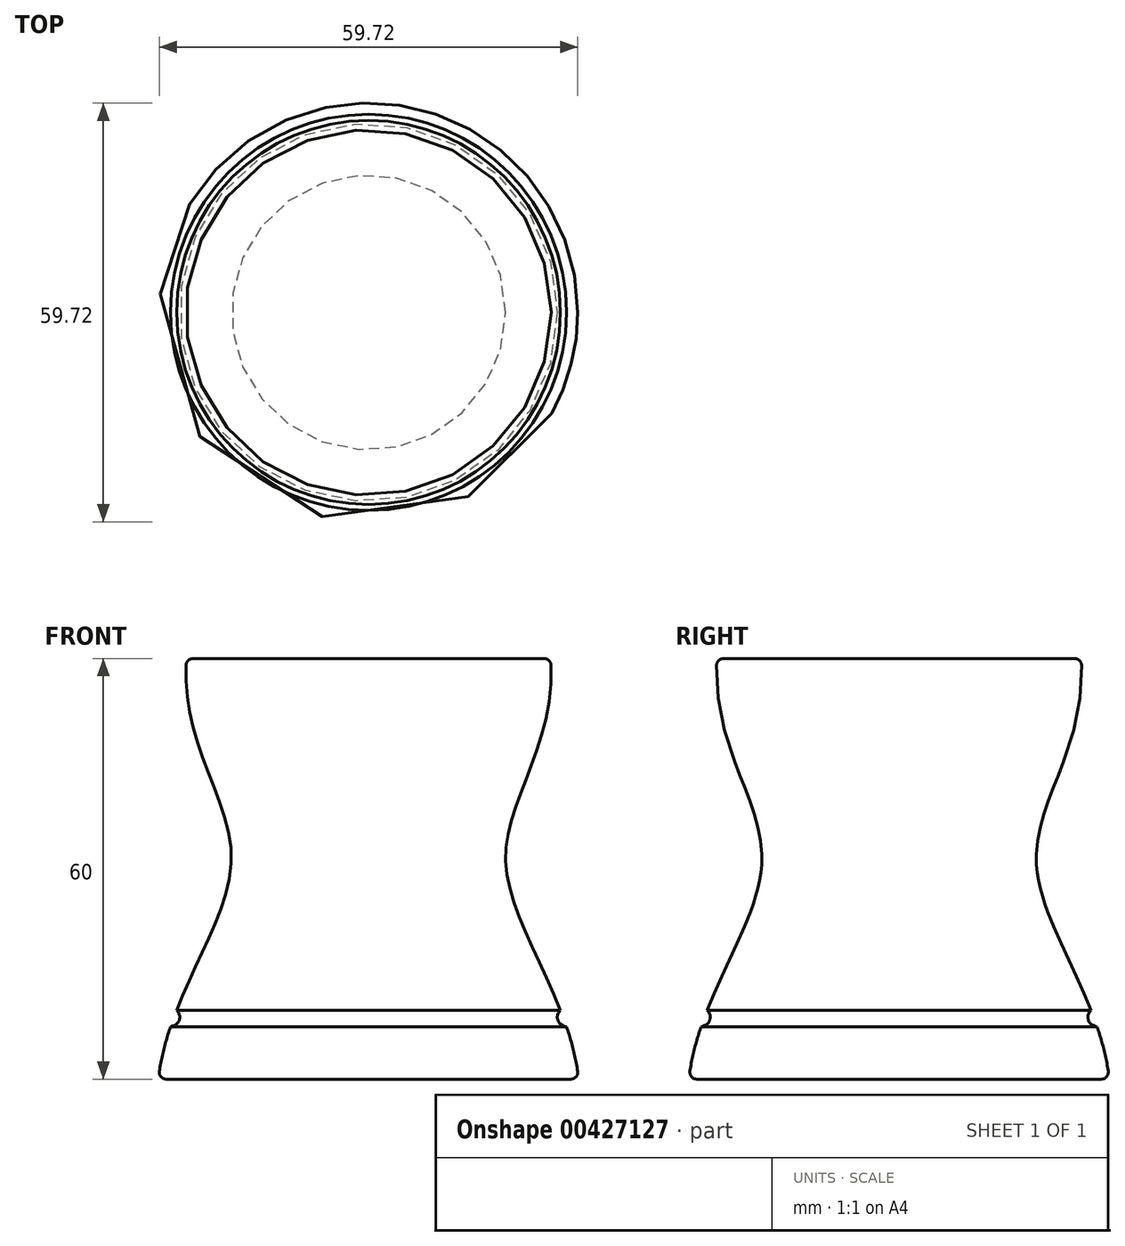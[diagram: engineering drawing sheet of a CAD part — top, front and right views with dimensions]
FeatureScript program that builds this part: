
annotation { "Feature Type Name" : "Feature", "Feature Type Description" : "" }
export const myFeature = defineFeature(function(context is Context, id is Id, definition is map)
    precondition{}
    {
        {
            var Q0;
            Q0=qCreatedBy(makeId("Front.planeOp"),FACE);
            var sketch = newSketch(context, id + "F0", { "sketchPlane" : qUnion([Q0])});
            skLineSegment(sketch, "E0", {"start": v(0, 0) * mm, "end": v(30, 0) * mm});
            skLineSegment(sketch, "E1", {"start": v(30, 0) * mm, "end": v(26, 60) * mm});
            skLineSegment(sketch, "E2", {"start": v(26, 60) * mm, "end": v(0, 60) * mm});
            skLineSegment(sketch, "E3", {"start": v(0, 60) * mm, "end": v(0, 0) * mm});
            skFitSpline(sketch, "E4", {"points": [v(26, 60) * mm, v(19.58, 31.17) * mm, v(30, 0) * mm], "startDerivative": vector(5.15, -77.25) * mm, "endDerivative": vector(7.58, -69.4) * mm});
            skFitSpline(sketch, "E5", {"points": [v(27.38, 9.85) * mm, v(27.04, 8.39) * mm, v(28.25, 7.5) * mm], "startDerivative": vector(-3.4, -4.24) * mm, "endDerivative": vector(5.59, -1.44) * mm});
            skSolve(sketch);
        }
        {
            var Q0;
            {var subQ3=sQuery(id+"F0.wireOp",EDGE,"E0");Q0=makeQuery(id+"F0.imprint","IMPRINT",FACE,{"disambiguationData":[TD([[makeQuery(id+"F0.imprint","IMPRINT",EDGE,{"derivedFrom":subQ3}),1.0]])]});}
            var Q1;
            Q1=sQuery(id+"F0.wireOp",EDGE,"E3");
            revolve(context, id + "F1", {"entities" : qUnion([Q0]), "axis" : qUnion([Q1]), "revolveType" : RevolveType.FULL});
        }
        {
            var Q0;
            Q0=makeQuery(id+"F1.opRevolve","SWEPT_EDGE",EDGE,{"disambiguationData":[OSD([sQuery(id+"F0.wireOp",EDGE,"E1"),sQuery(id+"F0.wireOp",EDGE,"E2"),sQuery(id+"F0.wireOp",EDGE,"E4")])]});
            var Q1;
            Q1=makeQuery(id+"F1.opRevolve","SWEPT_EDGE",EDGE,{"disambiguationData":[OSD([sQuery(id+"F0.wireOp",EDGE,"E0"),sQuery(id+"F0.wireOp",EDGE,"E1"),sQuery(id+"F0.wireOp",EDGE,"E4")])]});
            fillet(context, id + "F2", {"entities" : qUnion([Q0, Q1]), "radius" : 1 * mm, "tangentPropagation" : true, "allowEdgeOverflow" : false});
        }
    });
